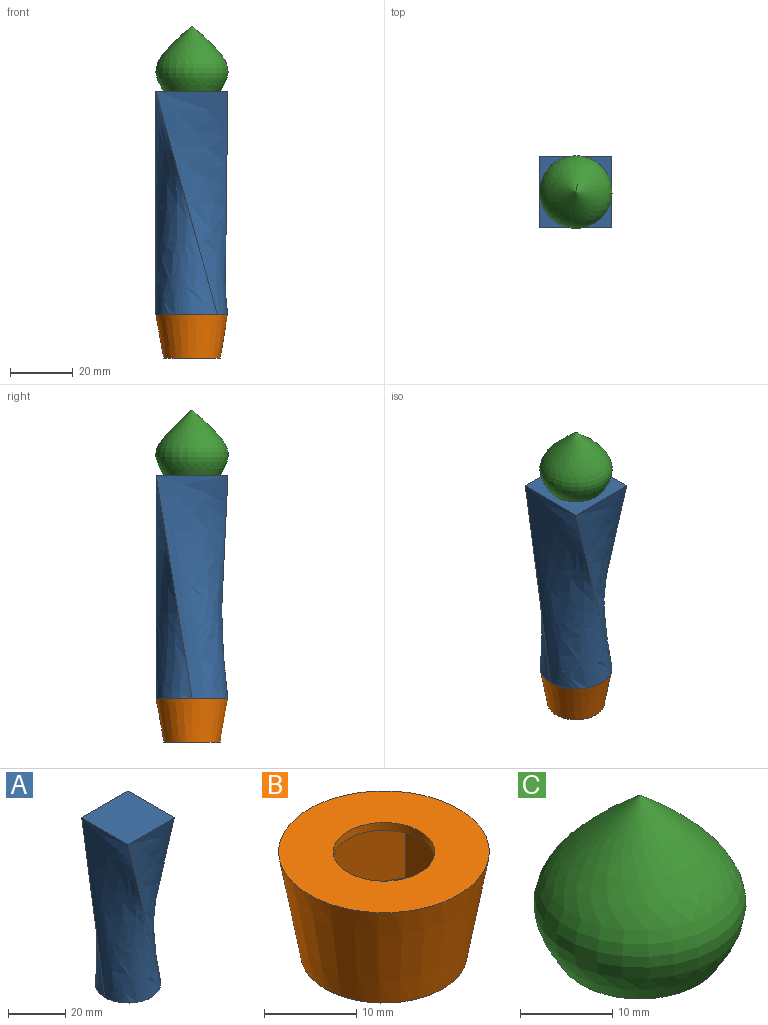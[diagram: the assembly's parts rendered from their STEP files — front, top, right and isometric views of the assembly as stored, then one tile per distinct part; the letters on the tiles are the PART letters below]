
ASSEMBLY  parts=3 mates=2
PART A: 8 faces, bbox 22.9x22.9x71.1 mm
  f0: plane 22.88x22.87mm, normal (0,0,-1), area 315.4mm2, adj f2,f3,f4,f5,f6
  f1: plane 22.86x22.86mm, normal (0,0,1), area 522.6mm2, adj f2,f3,f4,f5
  f2: bspline ~71.12x22.92mm, area 1112mm2, adj f0,f1,f3,f5
  f3: bspline ~71.12x22.87mm, area 1190.4mm2, adj f0,f1,f2,f4
  f4: bspline ~71.12x22.86mm, area 1356.2mm2, adj f0,f1,f3,f5
  f5: bspline ~71.12x22.92mm, area 1536mm2, adj f0,f1,f2,f4
  f6: cylinder r=5.5mm len=25.4mm, axis (0,0,-1), area 877.8mm2, adj f0,f7
  f7: plane 11x11mm, normal (0,0,-1), area 95mm2, adj f6
PART B: 13 faces, bbox 22.9x22.9x13.7 mm
  f0: cylinder r=5.5mm len=11mm, axis (0,0,-1), area 145.1mm2, adj f1,f5
  f1: plane 18x18mm, normal (0,0,-1), area 159.4mm2, adj f0,f2
  f2: cone r=11.43mm half-angle=10deg, axis (0,0,1), area 894mm2, adj f1,f3
  f3: plane 22.86x22.86mm, normal (0,0,1), area 315.4mm2, adj f2,f4
  f4: cylinder r=5.5mm len=11mm, axis (0,0,-1), area 35.1mm2, adj f3,f6
  f5: plane 17.78x15.4mm, normal (0,0,1), area 110.3mm2, adj f0,f7,f8,f9,f10,f11,f12
  f6: plane 17.78x15.4mm, normal (0,0,-1), area 110.3mm2, adj f4,f7,f8,f9,f10,f11,f12
  f7: plane 8.5x7.7mm, normal (-0.5,-0.87,0), area 75.6mm2, adj f5,f6,f8,f12
  f8: plane 8.5x7.7mm, normal (0.5,-0.87,0), area 75.6mm2, adj f5,f6,f7,f9
  f9: plane 8.89x8.5mm, normal (1,0,0), area 75.6mm2, adj f5,f6,f8,f10
  f10: plane 8.5x7.7mm, normal (0.5,0.87,0), area 75.6mm2, adj f5,f6,f9,f11
  f11: plane 8.5x7.7mm, normal (-0.5,0.87,0), area 75.6mm2, adj f5,f6,f10,f12
  f12: plane 8.89x8.5mm, normal (-1,0,0), area 75.6mm2, adj f5,f6,f7,f11
PART C: 2 faces, bbox 23.1x23.1x20.8 mm
  f0: plane 17.78x17.78mm, normal (0,0,-1), area 248.3mm2, adj f1
  f1: revolved ~23.08x23.08mm, area 1255.5mm2, adj f0
PLACE A t=(-60.64,-32.97,24.17)mm
PLACE B t=(17.47,-32.97,60.45)mm
PLACE C t=(-60.64,-63.18,193.93)mm
MATE fastened C.f0 <-> A.f6  axis (0,0,-1) through (-60.64,-32.97,145.29)mm
MATE fastened B.f0 <-> A.f6  axis (0,0,1) through (-60.64,-32.97,74.17)mm
